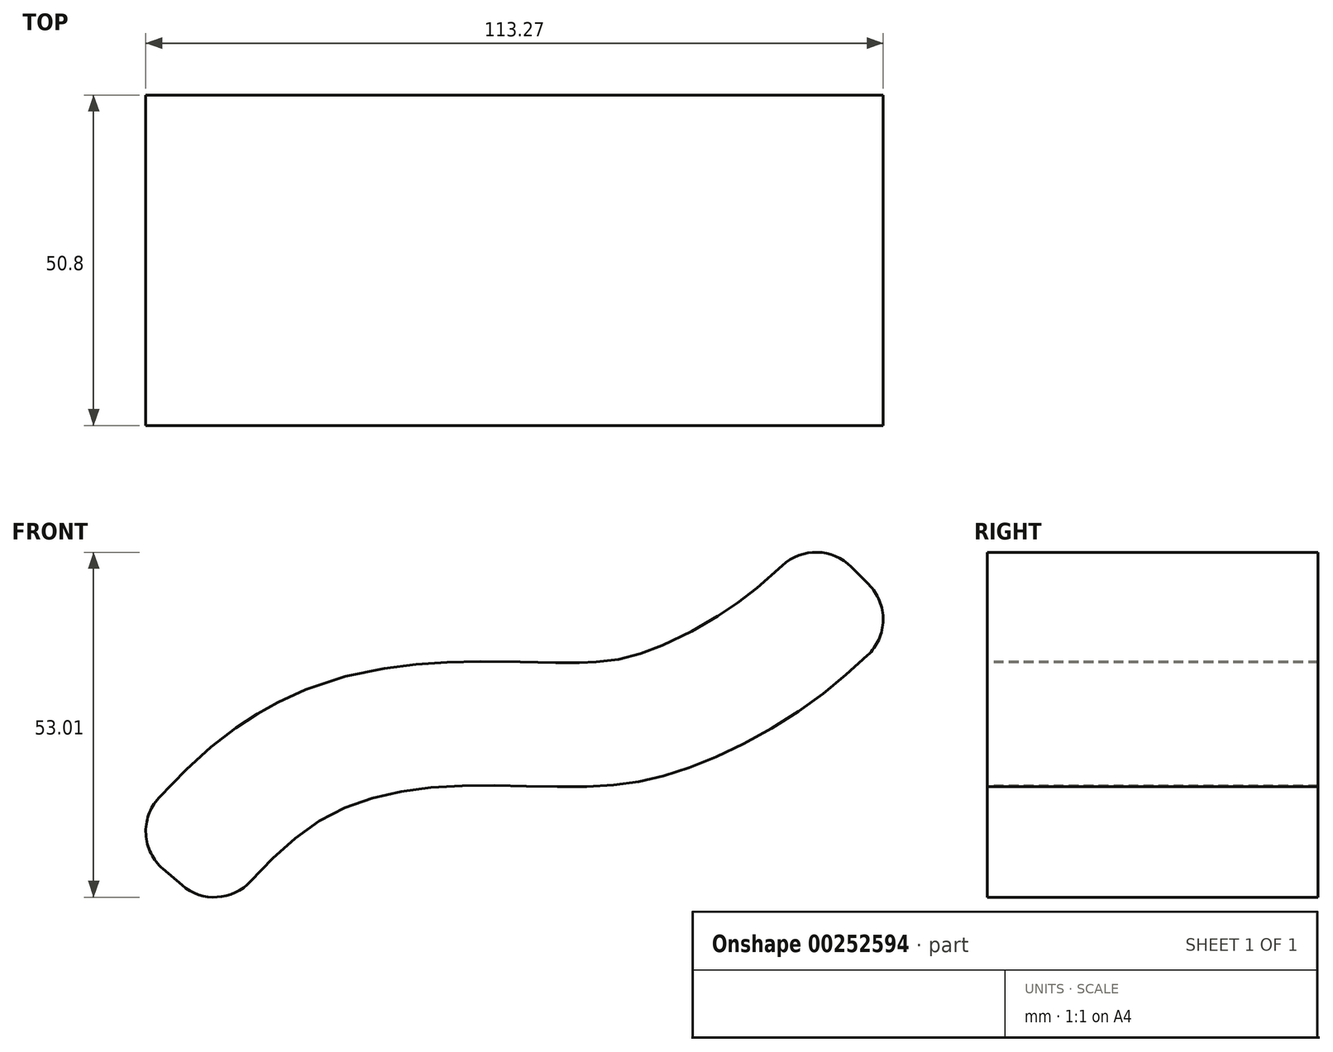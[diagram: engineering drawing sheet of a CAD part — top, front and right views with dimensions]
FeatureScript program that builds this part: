
annotation { "Feature Type Name" : "Feature", "Feature Type Description" : "" }
export const myFeature = defineFeature(function(context is Context, id is Id, definition is map)
    precondition{}
    {
        {
            var Q0;
            Q0=qCreatedBy(makeId("Front.planeOp"),FACE);
            var sketch = newSketch(context, id + "F0", { "sketchPlane" : qUnion([Q0])});
            skFitSpline(sketch, "E0", {"points": [v(-37.05, -20.1) * mm, v(-21.28, -5.12) * mm, v(-2.36, 0) * mm, v(19.7, 0) * mm, v(34.88, 2.76) * mm, v(53.8, 12.8) * mm, v(68.19, 25.62) * mm], "startDerivative": vector(85.18, 98.47) * mm, "endDerivative": vector(81.05, 80.75) * mm});
            skFitSpline(sketch, "E1.0", {"points": [v(-51.46, -7.64) * mm, v(-50.57, -6.61) * mm, v(-48.72, -4.47) * mm, v(-45.68, -1.08) * mm, v(-42.87, 1.83) * mm, v(-40.4, 4.18) * mm, v(-38.41, 5.93) * mm, v(-36.3, 7.66) * mm, v(-34.4, 9.06) * mm, v(-32.78, 10.15) * mm, v(-31.53, 10.95) * mm, v(-30.24, 11.72) * mm, v(-28.93, 12.44) * mm, v(-27.62, 13.12) * mm, v(-25.85, 13.96) * mm, v(-22.75, 15.28) * mm, v(-18.3, 16.76) * mm, v(-13.91, 17.76) * mm, v(-10.46, 18.33) * mm, v(-7.9, 18.66) * mm, v(-5.38, 18.9) * mm, v(-2.9, 19.06) * mm, v(-0.46, 19.16) * mm, v(2.7, 19.22) * mm, v(6.48, 19.2) * mm, v(10.69, 19.1) * mm, v(13.87, 19.03) * mm, v(16.17, 19) * mm, v(17.48, 19) * mm, v(18.45, 19.02) * mm, v(19.13, 19.04) * mm, v(19.76, 19.06) * mm, v(20.57, 19.1) * mm, v(21.5, 19.17) * mm, v(22.85, 19.3) * mm, v(24.35, 19.53) * mm, v(25.78, 19.86) * mm, v(27.02, 20.21) * mm, v(28.02, 20.53) * mm, v(29.12, 20.93) * mm, v(30.7, 21.55) * mm, v(32.87, 22.5) * mm, v(35.59, 23.87) * mm, v(37.86, 25.14) * mm, v(39.61, 26.21) * mm, v(40.89, 27.03) * mm, v(42.1, 27.86) * mm, v(43.25, 28.68) * mm, v(44.37, 29.54) * mm, v(45.85, 30.73) * mm, v(47.7, 32.32) * mm, v(50.69, 35.08) * mm, v(53.05, 37.43) * mm, v(54.74, 39.11) * mm]});
            skLineSegment(sketch, "E2", {"start": v(54.74, 39.11) * mm, "end": v(68.19, 25.62) * mm});
            skLineSegment(sketch, "E3", {"start": v(-51.46, -7.64) * mm, "end": v(-37.05, -20.1) * mm});
            skSolve(sketch);
        }
        {
            var Q0;
            Q0 = qSketchRegion(id + "F0", true);
            extrude(context, id + "F1", {"entities" : qUnion([Q0]), "depth" : 50.8 * mm});
        }
        {
            var Q0;
            Q0=makeQuery(id+"F1.opExtrude","SWEPT_EDGE",EDGE,{"disambiguationData":[OSD([sQuery(id+"F0.wireOp",EDGE,"E1.0"),sQuery(id+"F0.wireOp",EDGE,"E2")])]});
            var Q1;
            Q1=makeQuery(id+"F1.opExtrude","SWEPT_EDGE",EDGE,{"disambiguationData":[OSD([sQuery(id+"F0.wireOp",EDGE,"E0"),sQuery(id+"F0.wireOp",EDGE,"E2")])]});
            var Q2;
            Q2=makeQuery(id+"F1.opExtrude","SWEPT_EDGE",EDGE,{"disambiguationData":[OSD([sQuery(id+"F0.wireOp",EDGE,"E1.0"),sQuery(id+"F0.wireOp",EDGE,"E3")])]});
            var Q3;
            Q3=makeQuery(id+"F1.opExtrude","SWEPT_EDGE",EDGE,{"disambiguationData":[OSD([sQuery(id+"F0.wireOp",EDGE,"E0"),sQuery(id+"F0.wireOp",EDGE,"E3")])]});
            fillet(context, id + "F2", {"entities" : qUnion([Q0, Q1, Q2, Q3]), "radius" : 7.62 * mm, "tangentPropagation" : true, "allowEdgeOverflow" : false});
        }
    });
